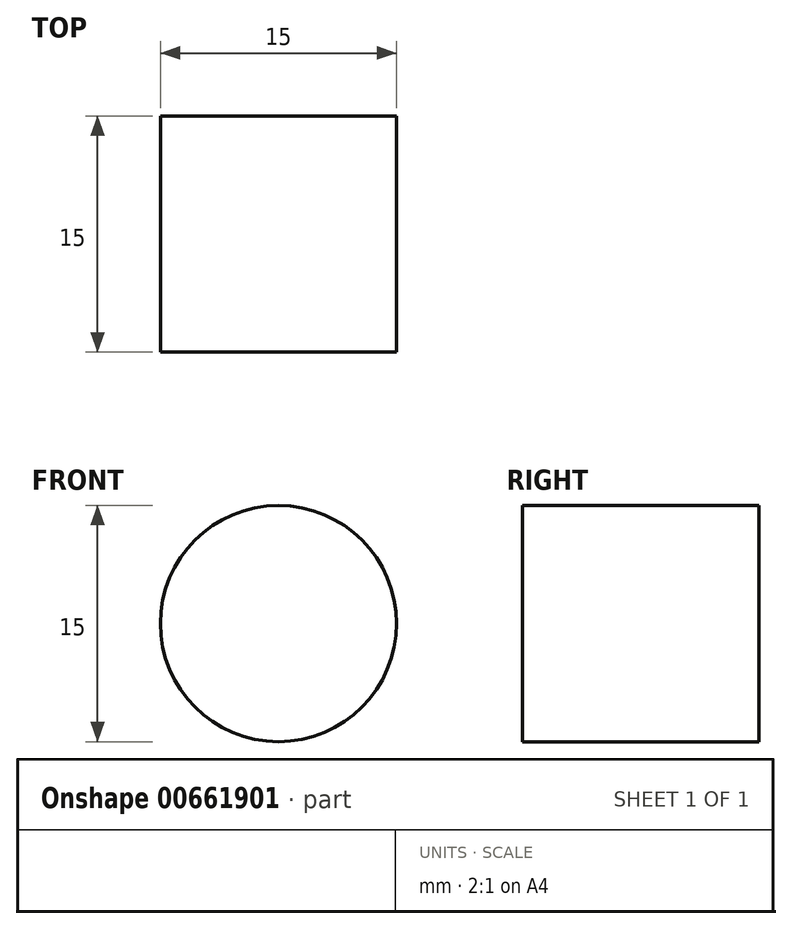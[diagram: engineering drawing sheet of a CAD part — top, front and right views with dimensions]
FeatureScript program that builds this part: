
annotation { "Feature Type Name" : "Feature", "Feature Type Description" : "" }
export const myFeature = defineFeature(function(context is Context, id is Id, definition is map)
    precondition{}
    {
        {
            var Q0;
            Q0=qCreatedBy(makeId("Front.planeOp"),FACE);
            var sketch = newSketch(context, id + "F0", { "sketchPlane" : qUnion([Q0])});
            skCircle(sketch, "E0", {"center": v(25.82, 27.47) * mm, "radius": 7.5 * mm});
            skSolve(sketch);
        }
        {
            var Q0;
            Q0 = qSketchRegion(id + "F0", true);
            extrude(context, id + "F1", {"entities" : qUnion([Q0]), "depth" : 15 * mm, "offsetDistance" : 25 * mm});
        }
    });
